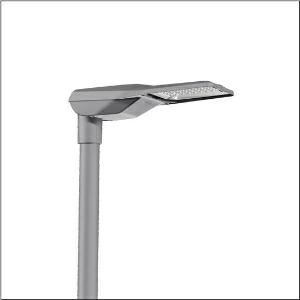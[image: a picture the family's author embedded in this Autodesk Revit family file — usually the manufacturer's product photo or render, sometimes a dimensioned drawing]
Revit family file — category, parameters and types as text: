
# Revit family: streetlight_sl_21_iq_mini___st1_5a_5xe2p41g08hb_3230
name_source: partatom
category: Lighting Fixtures
units: mm (PartAtom-declared; Revit-internal decimal feet)

## family parameters
Cut with Voids When Loaded = No
Host = Face
Light Source = No
Part Type = Normal
Room Calculation Point = No
Round Connector Dimension = Use Diameter
Shared = No

## types (1)
- --- (1 x LED, 9690 lm, 70.9 W, 4000K)
    Apparent Load = 71 VA
    CIE Flux Codes = 22 53 95 100 100
    Color Rendering = 70
    Color Temperature = 4000K
    Default Elevation = 1800 mm
    Description = Streetlight SL 21 iQ mini, mast luminaire, primary light control with lens, of PMMA, primary optical cover: cover, of toughened safety glass, transparent, light distribution: ST1.5a, light emission: direct distribution, primary light characteristic: asymmetric, installation type: post-top, side-entry, LED, High Power LED, rated luminous flux: 9.690lm, luminous efficacy: 137lm/W, light colour: 740, colour temperature: 4000K, control: Street-Remote, Auto-Match, Temp-Guard, Lumen-Switch, Night-Set, Smart-Wire, Light-Fading, Desk-Remote (wireless, voltage-free reading and setting of iQ features in the workshop via application-optimized NFC function/RFID function), optimised constant luminous flux control (CLO 2.0), presetting dimming linear, mains connection: 220..240V, AC, 50/60Hz, start of lifetime: 71W, end of service life: 75W, reduction: 31W, luminaire housing, of diecast aluminium, powder-coated, Siteco® metallic grey (DB 702S), corrosivity category C5 mid according to DIN EN ISO 12944, please order mast flange separately, inclination adjustable: 0°, 5°, 10°, 15°, sealing non-destructively replaceable, multi-level sealing system, length: 628mm, width: 235mm, height: 110mm, mast flange for spigot size: 42mm (side-entry): 5XC10008XM4, 60/48mm (side-entry/post-top): 5XC10108XM2, 76/60mm (side-entry/post-top): 5XC10108XM1, protection rating (complete): IP66, insulation class (complete): insulation class II (safety insulation), certification: CE, ENEC, ENEC+, VDE, impact resistance: IK09, permissible operating ambient temperature for outdoor applications: -40..+50°C, standard-compliant lighting for roads and squares, packaging unit: 1 piece

Light Distribution: ST1.5a
    Height = 110 mm
    Lamp = 1 x LED
    Lamp Light Flux = 9690 lm
    Lamp Power = 70.9 W
    Lamp count = 1
    Length = 625 mm
    Luminous efficacy = 137 lm/W
    Manufacturer = Siteco
    ModVariant = No
    Model = 5XE2P41G08HB
    Number of Poles = 1
    OnlyDefault = Yes
    Power Factor = 1
    Product Name = Streetlight SL 21 iQ mini | ST1.5a
    Product group = mast luminaire | pylon top
    ProductGroupID = 6100
    Protection Class = Protection class II
    Protection Degree = IP 66
    RLX_Detail_Level = 1
    RLX_Emergency_Light_Flux = 0 lm
    RLX_Emergency_Type = 0
    RLX_Emergency_Type_DB = No
    RlxData = <blob elided: 97605 chars, md5=bc89b080>
    Socket = socket
    Standby Power = 0 W
    System Light Flux = 9690 lm
    System Power = 71 W
    Type Comments = factory setting: luminous flux: 100 % | dim-lin: 254 | 711 mA
    Type Image = l_1003519.jpg
    URL = http://relux.com
    VarID = @adj_089317
    Voltage = 0 V
    Weight = 0.00 kg
    Width = 234 mm

## geometry (parser evidence)
native form markers: Blend x4, Sweep x9
no freeform markers — native parametric forms only
